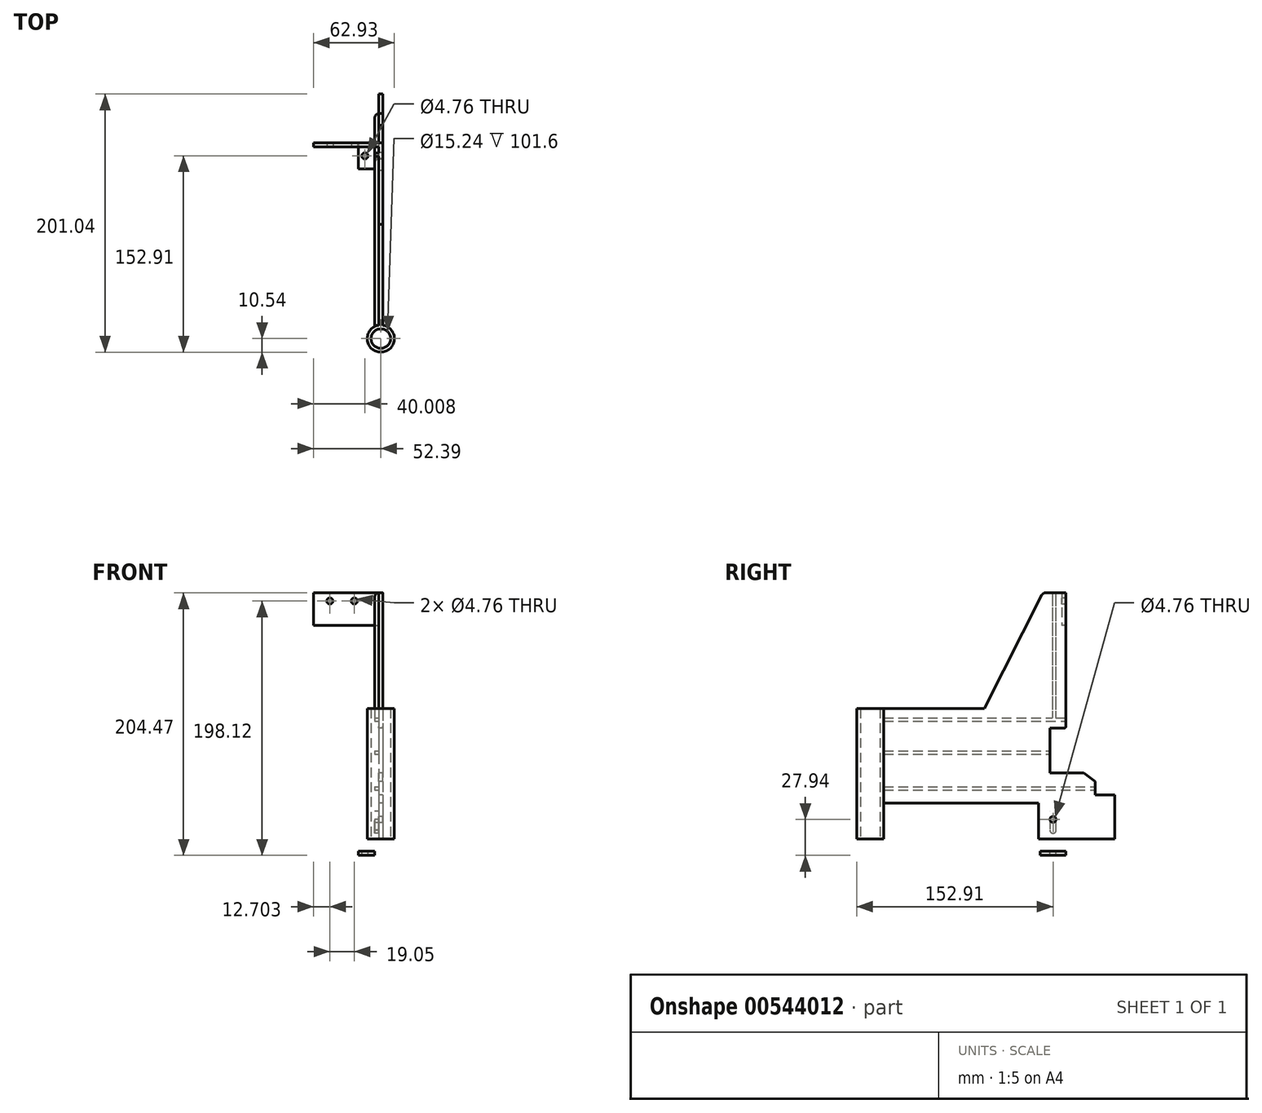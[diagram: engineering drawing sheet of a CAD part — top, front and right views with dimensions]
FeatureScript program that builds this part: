
annotation { "Feature Type Name" : "Feature", "Feature Type Description" : "" }
export const myFeature = defineFeature(function(context is Context, id is Id, definition is map)
    precondition{}
    {
        {
            var Q0;
            Q0=qCreatedBy(makeId("Top.planeOp"),FACE);
            var sketch = newSketch(context, id + "F0", { "sketchPlane" : qUnion([Q0])});
            skCircle(sketch, "E0", {"center": v(0, 0) * mm, "radius": 7.62 * mm});
            skLineSegment(sketch, "E1.bottom", {"start": v(-1.59, 190.5) * mm, "end": v(1.59, 190.5) * mm});
            skLineSegment(sketch, "E1.left", {"start": v(-1.59, 190.5) * mm, "end": v(-1.59, 7.45) * mm});
            skLineSegment(sketch, "E1.right", {"start": v(1.59, 190.5) * mm, "end": v(1.59, 7.45) * mm});
            skCircle(sketch, "E2", {"center": v(0, 0) * mm, "radius": 10.54 * mm});
            skPoint(sketch, "E3.orphan", {"position": v(-1.59, 0) * mm});
            skPoint(sketch, "E4.orphan", {"position": v(1.59, 0) * mm});
            skSolve(sketch);
        }
        {
            var Q0;
            {var subQ0=sQuery(id+"F0.wireOp",EDGE,"E1.left");var subQ1=sQuery(id+"F0.wireOp",EDGE,"E0");var subQ2=makeQuery(id+"F0.imprint","INTERSECT",VERTEX,{"derivedFrom":[subQ1,subQ0]});Q0=makeQuery(id+"F0.imprint","IMPRINT",FACE,{"disambiguationData":[TD([[makeQuery(id+"F0.imprint","IMPRINT",EDGE,{"disambiguationData":[TD([[subQ2,-1.0]])],"derivedFrom":subQ1}),-1.0]])]});}
            var Q1;
            {var subQ0=sQuery(id+"F0.wireOp",EDGE,"E1.left");var subQ1=sQuery(id+"F0.wireOp",EDGE,"E0");var subQ2=makeQuery(id+"F0.imprint","INTERSECT",VERTEX,{"derivedFrom":[subQ1,subQ0]});Q1=makeQuery(id+"F0.imprint","IMPRINT",FACE,{"disambiguationData":[TD([[makeQuery(id+"F0.imprint","IMPRINT",EDGE,{"disambiguationData":[TD([[subQ2,1.0]])],"derivedFrom":subQ1}),-1.0]])]});}
            var Q2;
            {var subQ0=sQuery(id+"F0.wireOp",EDGE,"E1.bottom");Q2=makeQuery(id+"F0.imprint","IMPRINT",FACE,{"disambiguationData":[TD([[makeQuery(id+"F0.imprint","IMPRINT",EDGE,{"derivedFrom":subQ0}),-1.0]])]});}
            extrude(context, id + "F1", {"entities" : qUnion([Q0, Q1, Q2]), "depth" : 101.6 * mm, "offsetDistance" : 25.4 * mm});
        }
        {
            var Q0;
            Q0=makeQuery(id+"F1.opExtrude","SWEPT_FACE",FACE,{"disambiguationData":[OSD([sQuery(id+"F0.wireOp",EDGE,"E1.left")])]});
            var sketch = newSketch(context, id + "F2", { "sketchPlane" : qUnion([Q0])});
            skLineSegment(sketch, "E5.bottom", {"start": v(-131.07, 27.94) * mm, "end": v(-10.42, 27.94) * mm});
            skLineSegment(sketch, "E5.top", {"start": v(-131.07, 0) * mm, "end": v(-10.42, 0) * mm});
            skLineSegment(sketch, "E5.left", {"start": v(-131.07, 27.94) * mm, "end": v(-131.07, 0) * mm});
            skLineSegment(sketch, "E5.right", {"start": v(-10.42, 27.94) * mm, "end": v(-10.42, 0) * mm});
            skSolve(sketch);
        }
        {
            var Q0;
            Q0=makeQuery(id+"F2.imprint","IMPRINT",FACE,{"disambiguationData":[TD([[makeQuery(id+"F2.imprint","IMPRINT",EDGE,{"derivedFrom":sQuery(id+"F2.wireOp",EDGE,"E5.bottom")}),-1.0]])]});
            var Q1;
            Q1=makeQuery(id+"F1.opExtrude","SWEPT_FACE",FACE,{"disambiguationData":[OSD([sQuery(id+"F0.wireOp",EDGE,"E1.right")])]});
            extrude(context, id + "F3", {"entities" : qUnion([Q0]), "operationType" : NewBodyOperationType.REMOVE, "endBound" : BoundingType.UP_TO_SURFACE, "oppositeDirection" : true, "depth" : 25.4 * mm, "endBoundEntityFace" : qUnion([Q1]), "offsetDistance" : 25.4 * mm});
        }
        {
            var Q0;
            Q0=makeQuery(id+"F1.opExtrude","SWEPT_FACE",FACE,{"disambiguationData":[OSD([sQuery(id+"F0.wireOp",EDGE,"E1.left")])]});
            var sketch = newSketch(context, id + "F4", { "sketchPlane" : qUnion([Q0])});
            skLineSegment(sketch, "E6.bottom", {"start": v(-222.67, 86.36) * mm, "end": v(-139.96, 86.36) * mm});
            skLineSegment(sketch, "E6.top", {"start": v(-222.67, 51.56) * mm, "end": v(-139.96, 51.56) * mm});
            skLineSegment(sketch, "E6.left", {"start": v(-222.67, 86.36) * mm, "end": v(-222.67, 51.56) * mm});
            skLineSegment(sketch, "E6.right", {"start": v(-139.96, 86.36) * mm, "end": v(-139.96, 51.56) * mm});
            skLineSegment(sketch, "E7.bottom", {"start": v(-190.5, 101.6) * mm, "end": v(-152.4, 101.6) * mm});
            skLineSegment(sketch, "E7.top", {"start": v(-190.5, 86.36) * mm, "end": v(-152.4, 86.36) * mm});
            skLineSegment(sketch, "E7.left", {"start": v(-190.5, 101.6) * mm, "end": v(-190.5, 86.36) * mm});
            skLineSegment(sketch, "E7.right", {"start": v(-152.4, 101.6) * mm, "end": v(-152.4, 86.36) * mm});
            skLineSegment(sketch, "E8.bottom", {"start": v(-199.94, 51.56) * mm, "end": v(-175.26, 51.56) * mm});
            skLineSegment(sketch, "E8.top", {"start": v(-199.94, 34.3) * mm, "end": v(-175.26, 34.3) * mm});
            skLineSegment(sketch, "E8.left", {"start": v(-199.94, 51.56) * mm, "end": v(-199.94, 34.3) * mm});
            skLineSegment(sketch, "E8.right", {"start": v(-175.26, 51.56) * mm, "end": v(-175.26, 34.3) * mm});
            skLineSegment(sketch, "E9", {"start": v(-175.26, 44.76) * mm, "end": v(-166.32, 51.56) * mm});
            skSolve(sketch);
        }
        {
            var Q0;
            {var subQ1=sQuery(id+"F4.wireOp",EDGE,"E6.right");Q0=makeQuery(id+"F4.imprint","IMPRINT",FACE,{"disambiguationData":[TD([[makeQuery(id+"F4.imprint","IMPRINT",EDGE,{"derivedFrom":subQ1}),-1.0]])]});}
            var Q1;
            Q1=makeQuery(id+"F4.imprint","IMPRINT",FACE,{"disambiguationData":[TD([[makeQuery(id+"F4.imprint","IMPRINT",EDGE,{"derivedFrom":sQuery(id+"F4.wireOp",EDGE,"E7.bottom")}),-1.0]])]});
            var Q2;
            {var subQ0=sQuery(id+"F4.wireOp",EDGE,"E8.right");var subQ4=sQuery(id+"F4.wireOp",EDGE,"E8.top");var subQ5=makeQuery(id+"F4.imprint","INTERSECT",VERTEX,{"derivedFrom":[subQ4,subQ0]});Q2=makeQuery(id+"F4.imprint","IMPRINT",FACE,{"disambiguationData":[TD([[makeQuery(id+"F4.imprint","IMPRINT",EDGE,{"disambiguationData":[TD([[subQ5,1.0]])],"derivedFrom":subQ0}),-1.0]])]});}
            var Q3;
            {var subQ3=sQuery(id+"F4.wireOp",EDGE,"E9");Q3=makeQuery(id+"F4.imprint","IMPRINT",FACE,{"disambiguationData":[TD([[makeQuery(id+"F4.imprint","IMPRINT",EDGE,{"derivedFrom":subQ3}),1.0]])]});}
            var Q4;
            Q4=makeQuery(id+"F1.opExtrude","SWEPT_FACE",FACE,{"disambiguationData":[OSD([sQuery(id+"F0.wireOp",EDGE,"E1.right")])]});
            extrude(context, id + "F5", {"entities" : qUnion([Q0, Q1, Q2, Q3]), "operationType" : NewBodyOperationType.REMOVE, "endBound" : BoundingType.UP_TO_SURFACE, "oppositeDirection" : true, "depth" : 25.4 * mm, "endBoundEntityFace" : qUnion([Q4]), "offsetDistance" : 25.4 * mm});
        }
        {
            var Q0;
            Q0=makeQuery(id+"F1.opExtrude","SWEPT_FACE",FACE,{"disambiguationData":[OSD([sQuery(id+"F0.wireOp",EDGE,"E1.left")])]});
            var sketch = newSketch(context, id + "F6", { "sketchPlane" : qUnion([Q0])});
            skLineSegment(sketch, "E10.bottom", {"start": v(-152.4, 101.6) * mm, "end": v(-88.9, 101.6) * mm});
            skLineSegment(sketch, "E10.top", {"start": v(-152.4, 191.77) * mm, "end": v(-88.9, 191.77) * mm});
            skLineSegment(sketch, "E10.left", {"start": v(-152.4, 101.6) * mm, "end": v(-152.4, 191.77) * mm});
            skLineSegment(sketch, "E10.right", {"start": v(-88.9, 101.6) * mm, "end": v(-88.9, 191.77) * mm});
            skLineSegment(sketch, "E11", {"start": v(-88.9, 101.6) * mm, "end": v(-134.62, 191.77) * mm});
            skSolve(sketch);
        }
        {
            var Q0;
            Q0=makeQuery(id+"F6.imprint","IMPRINT",FACE,{"disambiguationData":[TD([[makeQuery(id+"F6.imprint","IMPRINT",EDGE,{"derivedFrom":sQuery(id+"F6.wireOp",EDGE,"E10.bottom")}),1.0]])]});
            var Q1;
            Q1=makeQuery(id+"F1.opExtrude","SWEPT_FACE",FACE,{"disambiguationData":[OSD([sQuery(id+"F0.wireOp",EDGE,"E1.right")])]});
            extrude(context, id + "F7", {"entities" : qUnion([Q0]), "operationType" : NewBodyOperationType.ADD, "endBound" : BoundingType.UP_TO_SURFACE, "oppositeDirection" : true, "depth" : 25.4 * mm, "endBoundEntityFace" : qUnion([Q1]), "offsetDistance" : 25.4 * mm});
        }
        {
            var Q0;
            Q0=makeQuery(id+"F7.boolean.opBoolean","MERGE",FACE,{"derivedFrom":[makeQuery(id+"F1.opExtrude","SWEPT_FACE",FACE,{"disambiguationData":[OSD([sQuery(id+"F0.wireOp",EDGE,"E1.left")])]}),makeQuery(id+"F7.opExtrude","CAP_FACE",FACE,{"disambiguationData":[OSD([sQuery(id+"F6.wireOp",EDGE,"E10.bottom"),sQuery(id+"F6.wireOp",EDGE,"E10.top"),sQuery(id+"F6.wireOp",EDGE,"E10.left"),sQuery(id+"F6.wireOp",EDGE,"E11")])],"isStart":true})]});
            var sketch = newSketch(context, id + "F8", { "sketchPlane" : qUnion([Q0])});
            skLineSegment(sketch, "E12.bottom", {"start": v(-152.4, 191.77) * mm, "end": v(-149.23, 191.77) * mm});
            skLineSegment(sketch, "E12.top", {"start": v(-152.4, 166.37) * mm, "end": v(-149.23, 166.37) * mm});
            skLineSegment(sketch, "E12.left", {"start": v(-152.4, 191.77) * mm, "end": v(-152.4, 166.37) * mm});
            skLineSegment(sketch, "E12.right", {"start": v(-149.22, 191.77) * mm, "end": v(-149.22, 166.37) * mm});
            skSolve(sketch);
        }
        {
            var Q0;
            Q0=makeQuery(id+"F8.imprint","IMPRINT",FACE,{"disambiguationData":[TD([[makeQuery(id+"F8.imprint","IMPRINT",EDGE,{"derivedFrom":sQuery(id+"F8.wireOp",EDGE,"E12.bottom")}),-1.0]])]});
            extrude(context, id + "F9", {"entities" : qUnion([Q0]), "operationType" : NewBodyOperationType.ADD, "depth" : 50.8 * mm, "offsetDistance" : 25.4 * mm});
        }
        {
            var Q0;
            Q0=makeQuery(id+"F9.opExtrude","SWEPT_FACE",FACE,{"disambiguationData":[OSD([sQuery(id+"F8.wireOp",EDGE,"E12.right")])]});
            var sketch = newSketch(context, id + "F10", { "sketchPlane" : qUnion([Q0])});
            skCircle(sketch, "E13", {"center": v(-39.69, 185.42) * mm, "radius": 2.38 * mm});
            skCircle(sketch, "E14", {"center": v(-20.64, 185.42) * mm, "radius": 2.38 * mm});
            skPoint(sketch, "E15", {"position": v(-52.39, 179.07) * mm});
            skSolve(sketch);
        }
        {
            var Q0;
            Q0=makeQuery(id+"F10.imprint","IMPRINT",FACE,{"disambiguationData":[TD([[makeQuery(id+"F10.imprint","IMPRINT",EDGE,{"derivedFrom":sQuery(id+"F10.wireOp",EDGE,"E13")}),1.0]])]});
            var Q1;
            Q1=makeQuery(id+"F10.imprint","IMPRINT",FACE,{"disambiguationData":[TD([[makeQuery(id+"F10.imprint","IMPRINT",EDGE,{"derivedFrom":sQuery(id+"F10.wireOp",EDGE,"E14")}),1.0]])]});
            var Q2;
            Q2=makeQuery(id+"F9.boolean.opBoolean","MERGE",FACE,{"derivedFrom":[makeQuery(id+"F7.boolean.opBoolean","MERGE",FACE,{"derivedFrom":[makeQuery(id+"F5.boolean.opBoolean","COPY",FACE,{"derivedFrom":makeQuery(id+"F5.opExtrude","SWEPT_FACE",FACE,{"disambiguationData":[OSD([sQuery(id+"F4.wireOp",EDGE,"E7.right")])]})}),makeQuery(id+"F7.opExtrude","SWEPT_FACE",FACE,{"disambiguationData":[OSD([sQuery(id+"F6.wireOp",EDGE,"E10.left")])]})]}),makeQuery(id+"F9.opExtrude","SWEPT_FACE",FACE,{"disambiguationData":[OSD([sQuery(id+"F8.wireOp",EDGE,"E12.left")])]})]});
            var Q3;
            Q3=makeQuery(id+"F9.boolean.opBoolean","MERGE",FACE,{"derivedFrom":[makeQuery(id+"F7.boolean.opBoolean","MERGE",FACE,{"derivedFrom":[makeQuery(id+"F5.boolean.opBoolean","COPY",FACE,{"derivedFrom":makeQuery(id+"F5.opExtrude","SWEPT_FACE",FACE,{"disambiguationData":[OSD([sQuery(id+"F4.wireOp",EDGE,"E7.right")])]})}),makeQuery(id+"F7.opExtrude","SWEPT_FACE",FACE,{"disambiguationData":[OSD([sQuery(id+"F6.wireOp",EDGE,"E10.left")])]})]}),makeQuery(id+"F9.opExtrude","SWEPT_FACE",FACE,{"disambiguationData":[OSD([sQuery(id+"F8.wireOp",EDGE,"E12.left")])]})]});
            extrude(context, id + "F11", {"entities" : qUnion([Q0, Q1, Q2]), "operationType" : NewBodyOperationType.REMOVE, "oppositeDirection" : true, "depth" : 7.62 * mm, "endBoundEntityFace" : qUnion([Q3]), "offsetDistance" : 25.4 * mm});
        }
        {
            var Q0;
            Q0=makeQuery(id+"F7.boolean.opBoolean","MERGE",FACE,{"derivedFrom":[makeQuery(id+"F1.opExtrude","SWEPT_FACE",FACE,{"disambiguationData":[OSD([sQuery(id+"F0.wireOp",EDGE,"E1.left")])]}),makeQuery(id+"F7.opExtrude","CAP_FACE",FACE,{"disambiguationData":[OSD([sQuery(id+"F6.wireOp",EDGE,"E10.bottom"),sQuery(id+"F6.wireOp",EDGE,"E10.top"),sQuery(id+"F6.wireOp",EDGE,"E10.left"),sQuery(id+"F6.wireOp",EDGE,"E11")])],"isStart":true})]});
            var sketch = newSketch(context, id + "F12", { "sketchPlane" : qUnion([Q0])});
            skLineSegment(sketch, "E16.bottom", {"start": v(-10.42, 38.1) * mm, "end": v(-175.26, 38.1) * mm});
            skLineSegment(sketch, "E16.top", {"start": v(-10.42, 40.64) * mm, "end": v(-175.26, 40.64) * mm});
            skLineSegment(sketch, "E16.left", {"start": v(-10.42, 38.1) * mm, "end": v(-10.42, 40.64) * mm});
            skLineSegment(sketch, "E16.right", {"start": v(-175.26, 38.1) * mm, "end": v(-175.26, 40.64) * mm});
            skLineSegment(sketch, "E17.bottom", {"start": v(-10.42, 66.04) * mm, "end": v(-139.96, 66.04) * mm});
            skLineSegment(sketch, "E17.top", {"start": v(-10.42, 68.58) * mm, "end": v(-139.96, 68.58) * mm});
            skLineSegment(sketch, "E17.left", {"start": v(-10.42, 66.04) * mm, "end": v(-10.42, 68.58) * mm});
            skLineSegment(sketch, "E17.right", {"start": v(-139.96, 66.04) * mm, "end": v(-139.96, 68.58) * mm});
            skLineSegment(sketch, "E18.bottom", {"start": v(-10.42, 94.27) * mm, "end": v(-152.4, 94.27) * mm});
            skLineSegment(sketch, "E18.top", {"start": v(-10.42, 91.73) * mm, "end": v(-152.4, 91.73) * mm});
            skLineSegment(sketch, "E18.left", {"start": v(-10.42, 94.27) * mm, "end": v(-10.42, 91.73) * mm});
            skLineSegment(sketch, "E18.right", {"start": v(-152.4, 94.27) * mm, "end": v(-152.4, 91.73) * mm});
            skPoint(sketch, "E19.oppositeSnap0", {"position": v(-141.92, 191.77) * mm});
            skLineSegment(sketch, "E19.bottom", {"start": v(-144.46, 191.77) * mm, "end": v(-141.92, 191.77) * mm});
            skLineSegment(sketch, "E19.top", {"start": v(-144.46, 94.27) * mm, "end": v(-141.92, 94.27) * mm});
            skLineSegment(sketch, "E19.left", {"start": v(-144.46, 191.77) * mm, "end": v(-144.46, 94.27) * mm});
            skLineSegment(sketch, "E19.right", {"start": v(-141.92, 191.77) * mm, "end": v(-141.92, 94.27) * mm});
            skLineSegment(sketch, "E20.bottom", {"start": v(-120.98, 94.27) * mm, "end": v(-118.44, 94.27) * mm});
            skLineSegment(sketch, "E20.top", {"start": v(-120.98, 159.85) * mm, "end": v(-118.44, 159.85) * mm});
            skLineSegment(sketch, "E20.left", {"start": v(-120.98, 94.27) * mm, "end": v(-120.98, 159.85) * mm});
            skLineSegment(sketch, "E20.right", {"start": v(-118.44, 94.27) * mm, "end": v(-118.44, 159.85) * mm});
            skSolve(sketch);
        }
        {
            var Q0;
            Q0=makeQuery(id+"F12.imprint","IMPRINT",FACE,{"disambiguationData":[TD([[makeQuery(id+"F12.imprint","IMPRINT",EDGE,{"derivedFrom":sQuery(id+"F12.wireOp",EDGE,"E20.bottom")}),1.0]])]});
            var Q1;
            Q1=makeQuery(id+"F12.imprint","IMPRINT",FACE,{"disambiguationData":[TD([[makeQuery(id+"F12.imprint","IMPRINT",EDGE,{"derivedFrom":sQuery(id+"F12.wireOp",EDGE,"E19.bottom")}),-1.0]])]});
            var Q2;
            Q2=makeQuery(id+"F12.imprint","IMPRINT",FACE,{"disambiguationData":[TD([[makeQuery(id+"F12.imprint","IMPRINT",EDGE,{"derivedFrom":sQuery(id+"F12.wireOp",EDGE,"E18.top")}),-1.0]])]});
            var Q3;
            Q3=makeQuery(id+"F12.imprint","IMPRINT",FACE,{"disambiguationData":[TD([[makeQuery(id+"F12.imprint","IMPRINT",EDGE,{"derivedFrom":sQuery(id+"F12.wireOp",EDGE,"E17.bottom")}),-1.0]])]});
            var Q4;
            Q4=makeQuery(id+"F12.imprint","IMPRINT",FACE,{"disambiguationData":[TD([[makeQuery(id+"F12.imprint","IMPRINT",EDGE,{"derivedFrom":sQuery(id+"F12.wireOp",EDGE,"E16.bottom")}),-1.0]])]});
            extrude(context, id + "F13", {"entities" : qUnion([Q0, Q1, Q2, Q3, Q4]), "operationType" : NewBodyOperationType.ADD, "depth" : 3.05 * mm, "offsetDistance" : 25.4 * mm});
        }
        {
            var Q0;
            Q0=makeQuery(id+"F7.opExtrude","SWEPT_EDGE",EDGE,{"disambiguationData":[OSD([sQuery(id+"F6.wireOp",EDGE,"E10.top"),sQuery(id+"F6.wireOp",EDGE,"E11")])]});
            var Q1;
            Q1=makeQuery(id+"F13.opExtrude","CAP_EDGE",EDGE,{"disambiguationData":[OSD([sQuery(id+"F12.wireOp",EDGE,"E19.bottom")])],"isStart":false});
            var Q2;
            Q2=makeQuery(id+"F13.opExtrude","CAP_EDGE",EDGE,{"disambiguationData":[OSD([sQuery(id+"F12.wireOp",EDGE,"E18.right")])],"isStart":false});
            var Q3;
            Q3=makeQuery(id+"F13.opExtrude","CAP_EDGE",EDGE,{"disambiguationData":[OSD([sQuery(id+"F12.wireOp",EDGE,"E17.right")])],"isStart":false});
            var Q4;
            Q4=makeQuery(id+"F13.opExtrude","CAP_EDGE",EDGE,{"disambiguationData":[OSD([sQuery(id+"F12.wireOp",EDGE,"E20.top")])],"isStart":false});
            var Q5;
            Q5=makeQuery(id+"F13.opExtrude","CAP_EDGE",EDGE,{"disambiguationData":[OSD([sQuery(id+"F12.wireOp",EDGE,"E16.right")])],"isStart":false});
            fillet(context, id + "F14", {"entities" : qUnion([Q0, Q1, Q2, Q3, Q4, Q5]), "radius" : 3.05 * mm, "tangentPropagation" : true, "allowEdgeOverflow" : false});
        }
        {
            var Q0;
            Q0=makeQuery(id+"F5.boolean.opBoolean","COPY",EDGE,{"derivedFrom":makeQuery(id+"F5.opExtrude","CAP_EDGE",EDGE,{"disambiguationData":[OSD([sQuery(id+"F4.wireOp",EDGE,"E9")])],"isStart":true})});
            var Q1;
            Q1=makeQuery(id+"F5.boolean.opBoolean","COPY",EDGE,{"derivedFrom":makeQuery(id+"F5.opExtrude","CAP_EDGE",EDGE,{"disambiguationData":[OSD([sQuery(id+"F4.wireOp",EDGE,"E6.top")])],"isStart":true})});
            var Q2;
            Q2=makeQuery(id+"F5.boolean.opBoolean","COPY",EDGE,{"derivedFrom":makeQuery(id+"F5.opExtrude","CAP_EDGE",EDGE,{"disambiguationData":[OSD([sQuery(id+"F4.wireOp",EDGE,"E8.top")])],"isStart":true})});
            var Q3;
            {var subQ0=sQuery(id+"F4.wireOp",EDGE,"E8.right");Q3=makeQuery(id+"F13.boolean.opBoolean","SPLIT",EDGE,{"disambiguationData":[TD([makeQuery(id+"F5.boolean.opBoolean","COPY",FACE,{"derivedFrom":makeQuery(id+"F5.opExtrude","SWEPT_FACE",FACE,{"disambiguationData":[OSD([sQuery(id+"F4.wireOp",EDGE,"E8.top")])]})})])],"derivedFrom":makeQuery(id+"F5.boolean.opBoolean","COPY",EDGE,{"derivedFrom":makeQuery(id+"F5.opExtrude","CAP_EDGE",EDGE,{"disambiguationData":[OSD([subQ0])],"isStart":true})})});}
            var Q4;
            {var subQ0=sQuery(id+"F4.wireOp",EDGE,"E8.right");Q4=makeQuery(id+"F13.boolean.opBoolean","SPLIT",EDGE,{"disambiguationData":[TD([makeQuery(id+"F5.boolean.opBoolean","COPY",FACE,{"derivedFrom":makeQuery(id+"F5.opExtrude","SWEPT_FACE",FACE,{"disambiguationData":[OSD([sQuery(id+"F4.wireOp",EDGE,"E9")])]})})])],"derivedFrom":makeQuery(id+"F5.boolean.opBoolean","COPY",EDGE,{"derivedFrom":makeQuery(id+"F5.opExtrude","CAP_EDGE",EDGE,{"disambiguationData":[OSD([subQ0])],"isStart":true})})});}
            var Q5;
            Q5=makeQuery(id+"F5.boolean.opBoolean","COPY",EDGE,{"derivedFrom":makeQuery(id+"F5.opExtrude","CAP_EDGE",EDGE,{"disambiguationData":[OSD([sQuery(id+"F4.wireOp",EDGE,"E8.top")])],"isStart":false})});
            var Q6;
            Q6=makeQuery(id+"F5.boolean.opBoolean","COPY",EDGE,{"derivedFrom":makeQuery(id+"F5.opExtrude","CAP_EDGE",EDGE,{"disambiguationData":[OSD([sQuery(id+"F4.wireOp",EDGE,"E8.right")])],"isStart":false})});
            var Q7;
            Q7=makeQuery(id+"F5.boolean.opBoolean","COPY",EDGE,{"derivedFrom":makeQuery(id+"F5.opExtrude","CAP_EDGE",EDGE,{"disambiguationData":[OSD([sQuery(id+"F4.wireOp",EDGE,"E9")])],"isStart":false})});
            var Q8;
            Q8=makeQuery(id+"F5.boolean.opBoolean","COPY",EDGE,{"derivedFrom":makeQuery(id+"F5.opExtrude","CAP_EDGE",EDGE,{"disambiguationData":[OSD([sQuery(id+"F4.wireOp",EDGE,"E6.top")])],"isStart":false})});
            var Q9;
            {var subQ0=sQuery(id+"F4.wireOp",EDGE,"E6.right");Q9=makeQuery(id+"F13.boolean.opBoolean","SPLIT",EDGE,{"disambiguationData":[TD([makeQuery(id+"F5.boolean.opBoolean","COPY",FACE,{"derivedFrom":makeQuery(id+"F5.opExtrude","SWEPT_FACE",FACE,{"disambiguationData":[OSD([sQuery(id+"F4.wireOp",EDGE,"E6.top")])]})})])],"derivedFrom":makeQuery(id+"F5.boolean.opBoolean","COPY",EDGE,{"derivedFrom":makeQuery(id+"F5.opExtrude","CAP_EDGE",EDGE,{"disambiguationData":[OSD([subQ0])],"isStart":true})})});}
            var Q10;
            {var subQ0=sQuery(id+"F4.wireOp",EDGE,"E6.right");Q10=makeQuery(id+"F13.boolean.opBoolean","SPLIT",EDGE,{"disambiguationData":[TD([makeQuery(id+"F5.boolean.opBoolean","COPY",FACE,{"derivedFrom":makeQuery(id+"F5.opExtrude","SWEPT_FACE",FACE,{"disambiguationData":[OSD([sQuery(id+"F4.wireOp",EDGE,"E6.bottom")])]})})])],"derivedFrom":makeQuery(id+"F5.boolean.opBoolean","COPY",EDGE,{"derivedFrom":makeQuery(id+"F5.opExtrude","CAP_EDGE",EDGE,{"disambiguationData":[OSD([subQ0])],"isStart":true})})});}
            var Q11;
            Q11=makeQuery(id+"F5.boolean.opBoolean","COPY",EDGE,{"derivedFrom":makeQuery(id+"F5.opExtrude","CAP_EDGE",EDGE,{"disambiguationData":[OSD([sQuery(id+"F4.wireOp",EDGE,"E6.right")])],"isStart":false})});
            var Q12;
            Q12=makeQuery(id+"F5.boolean.opBoolean","COPY",EDGE,{"derivedFrom":makeQuery(id+"F5.opExtrude","CAP_EDGE",EDGE,{"disambiguationData":[OSD([sQuery(id+"F4.wireOp",EDGE,"E6.bottom")])],"isStart":true})});
            var Q13;
            Q13=makeQuery(id+"F5.boolean.opBoolean","COPY",EDGE,{"derivedFrom":makeQuery(id+"F5.opExtrude","CAP_EDGE",EDGE,{"disambiguationData":[OSD([sQuery(id+"F4.wireOp",EDGE,"E6.bottom")])],"isStart":false})});
            var Q14;
            Q14=makeQuery(id+"F5.boolean.opBoolean","COPY",EDGE,{"derivedFrom":makeQuery(id+"F5.opExtrude","SWEPT_EDGE",EDGE,{"disambiguationData":[OSD([sQuery(id+"F4.wireOp",EDGE,"E6.bottom"),sQuery(id+"F4.wireOp",EDGE,"E7.top"),sQuery(id+"F4.wireOp",EDGE,"E7.right")])]})});
            var Q15;
            Q15=makeQuery(id+"F3.boolean.opBoolean","COPY",EDGE,{"derivedFrom":makeQuery(id+"F3.opExtrude","CAP_EDGE",EDGE,{"disambiguationData":[OSD([sQuery(id+"F2.wireOp",EDGE,"E5.bottom")])],"isStart":false})});
            var Q16;
            Q16=makeQuery(id+"F3.boolean.opBoolean","COPY",EDGE,{"derivedFrom":makeQuery(id+"F3.opExtrude","CAP_EDGE",EDGE,{"disambiguationData":[OSD([sQuery(id+"F2.wireOp",EDGE,"E5.bottom")])],"isStart":true})});
            var Q17;
            Q17=makeQuery(id+"F3.boolean.opBoolean","COPY",EDGE,{"derivedFrom":makeQuery(id+"F3.opExtrude","CAP_EDGE",EDGE,{"disambiguationData":[OSD([sQuery(id+"F2.wireOp",EDGE,"E5.left")])],"isStart":false})});
            var Q18;
            Q18=makeQuery(id+"F3.boolean.opBoolean","COPY",EDGE,{"derivedFrom":makeQuery(id+"F3.opExtrude","CAP_EDGE",EDGE,{"disambiguationData":[OSD([sQuery(id+"F2.wireOp",EDGE,"E5.left")])],"isStart":true})});
            fillet(context, id + "F15", {"entities" : qUnion([Q0, Q1, Q2, Q3, Q4, Q5, Q6, Q7, Q8, Q9, Q10, Q11, Q12, Q13, Q14, Q15, Q16, Q17, Q18]), "radius" : 1.27 * mm, "tangentPropagation" : true, "allowEdgeOverflow" : false});
        }
        {
            var Q0;
            {var subQ1=sQuery(id+"F0.wireOp",EDGE,"E1.left");var subQ2=sQuery(id+"F0.wireOp",EDGE,"E1.bottom");Q0=makeQuery(id+"F13.boolean.opBoolean","SPLIT",FACE,{"disambiguationData":[TD([makeQuery(id+"F1.opExtrude","SWEPT_FACE",FACE,{"disambiguationData":[OSD([subQ2])]})])],"derivedFrom":makeQuery(id+"F7.boolean.opBoolean","MERGE",FACE,{"derivedFrom":[makeQuery(id+"F1.opExtrude","SWEPT_FACE",FACE,{"disambiguationData":[OSD([subQ1])]}),makeQuery(id+"F7.opExtrude","CAP_FACE",FACE,{"disambiguationData":[OSD([sQuery(id+"F6.wireOp",EDGE,"E10.bottom"),sQuery(id+"F6.wireOp",EDGE,"E10.top"),sQuery(id+"F6.wireOp",EDGE,"E10.left"),sQuery(id+"F6.wireOp",EDGE,"E11")])],"isStart":true})]})});}
            var sketch = newSketch(context, id + "F16", { "sketchPlane" : qUnion([Q0])});
            skLineSegment(sketch, "E21.bottom", {"start": v(-152.4, 27.94) * mm, "end": v(-132.34, 27.94) * mm});
            skLineSegment(sketch, "E21.top", {"start": v(-152.4, -12.7) * mm, "end": v(-132.34, -12.7) * mm});
            skLineSegment(sketch, "E21.left", {"start": v(-152.4, 27.94) * mm, "end": v(-152.4, -12.7) * mm});
            skLineSegment(sketch, "E21.right", {"start": v(-132.34, 27.94) * mm, "end": v(-132.34, -12.7) * mm});
            skSolve(sketch);
        }
        {
            var Q0;
            {var subQ0=sQuery(id+"F16.wireOp",EDGE,"E21.bottom");Q0=makeQuery(id+"F16.imprint","IMPRINT",FACE,{"disambiguationData":[TD([[makeQuery(id+"F16.imprint","IMPRINT",EDGE,{"derivedFrom":subQ0}),-1.0]])]});}
            var Q1;
            {var subQ0=sQuery(id+"F16.wireOp",EDGE,"E21.top");Q1=makeQuery(id+"F16.imprint","IMPRINT",FACE,{"disambiguationData":[TD([[makeQuery(id+"F16.imprint","IMPRINT",EDGE,{"derivedFrom":subQ0}),1.0]])]});}
            extrude(context, id + "F17", {"entities" : qUnion([Q0, Q1]), "depth" : 3.17 * mm, "offsetDistance" : 25.4 * mm});
        }
        {
            var Q0;
            Q0=makeQuery(id+"F17.opExtrude","CAP_FACE",FACE,{"disambiguationData":[OSD([sQuery(id+"F16.wireOp",EDGE,"E21.bottom"),sQuery(id+"F16.wireOp",EDGE,"E21.top"),sQuery(id+"F16.wireOp",EDGE,"E21.left"),sQuery(id+"F16.wireOp",EDGE,"E21.right")])],"isStart":false});
            var sketch = newSketch(context, id + "F18", { "sketchPlane" : qUnion([Q0])});
            skCircle(sketch, "E22", {"center": v(-142.37, 15.24) * mm, "radius": 2.38 * mm});
            skPoint(sketch, "E23", {"position": v(-142.37, 27.94) * mm});
            skSolve(sketch);
        }
        {
            var Q0;
            Q0=makeQuery(id+"F18.imprint","IMPRINT",FACE,{"disambiguationData":[TD([[makeQuery(id+"F18.imprint","IMPRINT",EDGE,{"derivedFrom":sQuery(id+"F18.wireOp",EDGE,"E22")}),1.0]])]});
            extrude(context, id + "F19", {"entities" : qUnion([Q0]), "operationType" : NewBodyOperationType.REMOVE, "oppositeDirection" : true, "depth" : 25.4 * mm, "offsetDistance" : 25.4 * mm});
        }
        {
            var Q0;
            Q0=makeQuery(id+"F17.opExtrude","CAP_FACE",FACE,{"disambiguationData":[OSD([sQuery(id+"F16.wireOp",EDGE,"E21.bottom"),sQuery(id+"F16.wireOp",EDGE,"E21.top"),sQuery(id+"F16.wireOp",EDGE,"E21.left"),sQuery(id+"F16.wireOp",EDGE,"E21.right")])],"isStart":false});
            var sketch = newSketch(context, id + "F20", { "sketchPlane" : qUnion([Q0])});
            skCircle(sketch, "E24", {"center": v(-142.37, 21.6) * mm, "radius": 2.38 * mm});
            skCircle(sketch, "E25", {"center": v(-142.37, 6.86) * mm, "radius": 2.38 * mm});
            skLineSegment(sketch, "E26", {"start": v(-144.75, 6.75) * mm, "end": v(-144.75, 21.7) * mm});
            skLineSegment(sketch, "E27", {"start": v(-144.75, 21.7) * mm, "end": v(-140, 21.7) * mm});
            skLineSegment(sketch, "E28", {"start": v(-140, 21.7) * mm, "end": v(-140, 6.75) * mm});
            skSolve(sketch);
        }
        {
            var Q0;
            {var subQ5=sQuery(id+"F20.wireOp",EDGE,"E27");Q0=makeQuery(id+"F20.imprint","IMPRINT",FACE,{"disambiguationData":[TD([[makeQuery(id+"F20.imprint","IMPRINT",EDGE,{"derivedFrom":subQ5}),-1.0]])]});}
            var Q1;
            {var subQ0=sQuery(id+"F20.wireOp",EDGE,"E27");Q1=makeQuery(id+"F20.imprint","IMPRINT",FACE,{"disambiguationData":[TD([[makeQuery(id+"F20.imprint","IMPRINT",EDGE,{"derivedFrom":subQ0}),1.0]])]});}
            var Q2;
            {var subQ0=sQuery(id+"F20.wireOp",EDGE,"E26");var subQ1=sQuery(id+"F20.wireOp",EDGE,"E24");var subQ2=makeQuery(id+"F20.imprint","INTERSECT",VERTEX,{"derivedFrom":[subQ1,subQ0]});Q2=makeQuery(id+"F20.imprint","IMPRINT",FACE,{"disambiguationData":[TD([[makeQuery(id+"F20.imprint","IMPRINT",EDGE,{"disambiguationData":[TD([[subQ2,-1.0]])],"derivedFrom":subQ1}),-1.0]])]});}
            var Q3;
            {var subQ0=sQuery(id+"F20.wireOp",EDGE,"E26");var subQ1=sQuery(id+"F20.wireOp",EDGE,"E25");var subQ2=makeQuery(id+"F20.imprint","INTERSECT",VERTEX,{"disambiguationData":[OD(1.0)],"derivedFrom":[subQ1,subQ0]});Q3=makeQuery(id+"F20.imprint","IMPRINT",FACE,{"disambiguationData":[TD([[makeQuery(id+"F20.imprint","IMPRINT",EDGE,{"disambiguationData":[TD([[subQ2,1.0]])],"derivedFrom":subQ1}),-1.0]])]});}
            var Q4;
            {var subQ0=sQuery(id+"F20.wireOp",EDGE,"E26");var subQ1=sQuery(id+"F20.wireOp",EDGE,"E25");var subQ2=makeQuery(id+"F20.imprint","INTERSECT",VERTEX,{"disambiguationData":[OD(0.0)],"derivedFrom":[subQ1,subQ0]});Q4=makeQuery(id+"F20.imprint","IMPRINT",FACE,{"disambiguationData":[TD([[makeQuery(id+"F20.imprint","IMPRINT",EDGE,{"disambiguationData":[TD([[subQ2,-1.0]])],"derivedFrom":subQ1}),1.0]])]});}
            var Q5;
            Q5=makeQuery(id+"F17.opExtrude","CAP_FACE",FACE,{"disambiguationData":[OSD([sQuery(id+"F16.wireOp",EDGE,"E21.bottom"),sQuery(id+"F16.wireOp",EDGE,"E21.top"),sQuery(id+"F16.wireOp",EDGE,"E21.left"),sQuery(id+"F16.wireOp",EDGE,"E21.right")])],"isStart":true});
            extrude(context, id + "F21", {"entities" : qUnion([Q0, Q1, Q2, Q3, Q4]), "operationType" : NewBodyOperationType.REMOVE, "endBound" : BoundingType.UP_TO_SURFACE, "oppositeDirection" : true, "depth" : 25.4 * mm, "endBoundEntityFace" : qUnion([Q5]), "offsetDistance" : 25.4 * mm});
        }
        {
            var Q0;
            Q0=makeQuery(id+"F17.opExtrude","CAP_FACE",FACE,{"disambiguationData":[OSD([sQuery(id+"F16.wireOp",EDGE,"E21.bottom"),sQuery(id+"F16.wireOp",EDGE,"E21.top"),sQuery(id+"F16.wireOp",EDGE,"E21.left"),sQuery(id+"F16.wireOp",EDGE,"E21.right")])],"isStart":false});
            var sketch = newSketch(context, id + "F22", { "sketchPlane" : qUnion([Q0])});
            skLineSegment(sketch, "E29.bottom", {"start": v(-152.4, -12.7) * mm, "end": v(-132.34, -12.7) * mm});
            skLineSegment(sketch, "E29.top", {"start": v(-152.4, -9.53) * mm, "end": v(-132.34, -9.53) * mm});
            skLineSegment(sketch, "E29.left", {"start": v(-152.4, -12.7) * mm, "end": v(-152.4, -9.53) * mm});
            skLineSegment(sketch, "E29.right", {"start": v(-132.34, -12.7) * mm, "end": v(-132.34, -9.53) * mm});
            skSolve(sketch);
        }
        {
            var Q0;
            Q0=makeQuery(id+"F22.imprint","IMPRINT",FACE,{"disambiguationData":[TD([[makeQuery(id+"F22.imprint","IMPRINT",EDGE,{"derivedFrom":sQuery(id+"F22.wireOp",EDGE,"E29.bottom")}),1.0]])]});
            extrude(context, id + "F23", {"entities" : qUnion([Q0]), "operationType" : NewBodyOperationType.ADD, "depth" : 12.7 * mm, "offsetDistance" : 25.4 * mm});
        }
        {
            var Q0;
            Q0=makeQuery(id+"F23.opExtrude","SWEPT_FACE",FACE,{"disambiguationData":[OSD([sQuery(id+"F22.wireOp",EDGE,"E29.top")])]});
            var sketch = newSketch(context, id + "F24", { "sketchPlane" : qUnion([Q0])});
            skCircle(sketch, "E30", {"center": v(-12.38, 142.37) * mm, "radius": 2.38 * mm});
            skPoint(sketch, "E31", {"position": v(-17.46, 142.37) * mm});
            skSolve(sketch);
        }
        {
            var Q0;
            Q0=makeQuery(id+"F24.imprint","IMPRINT",FACE,{"disambiguationData":[TD([[makeQuery(id+"F24.imprint","IMPRINT",EDGE,{"derivedFrom":sQuery(id+"F24.wireOp",EDGE,"E30")}),1.0]])]});
            extrude(context, id + "F25", {"entities" : qUnion([Q0]), "operationType" : NewBodyOperationType.REMOVE, "oppositeDirection" : true, "depth" : 25.4 * mm, "offsetDistance" : 25.4 * mm});
        }
    });
